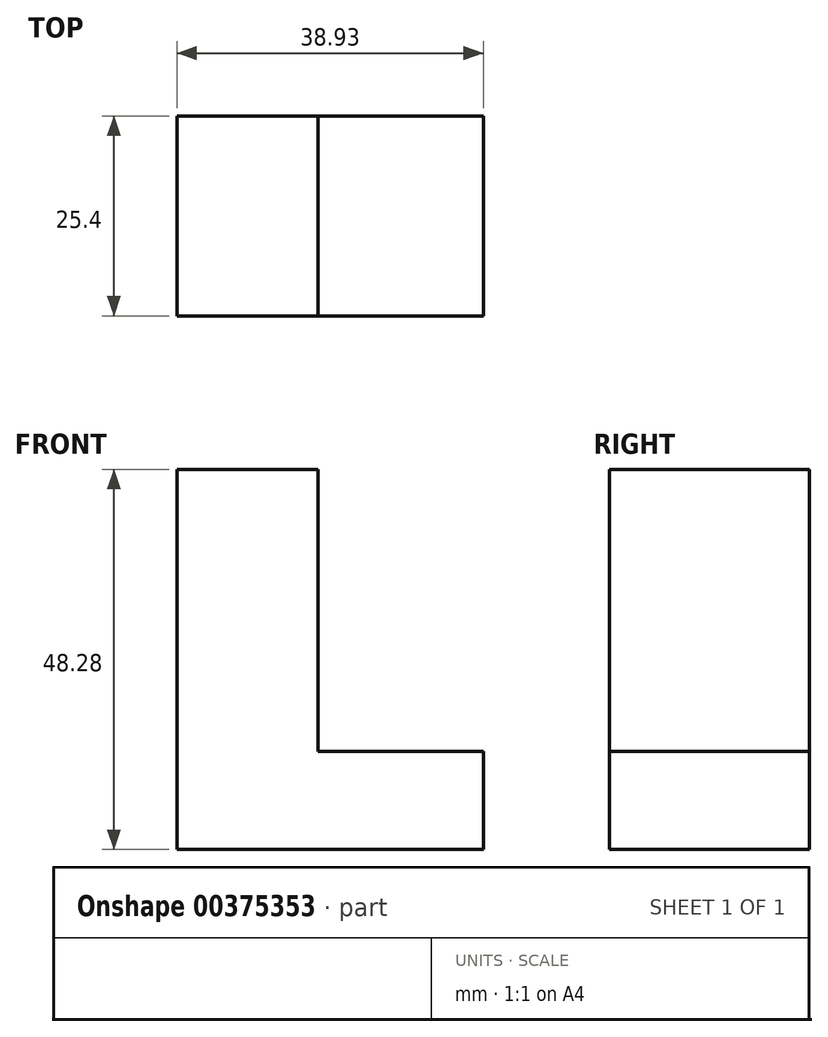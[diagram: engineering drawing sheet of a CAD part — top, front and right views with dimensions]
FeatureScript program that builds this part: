
annotation { "Feature Type Name" : "Feature", "Feature Type Description" : "" }
export const myFeature = defineFeature(function(context is Context, id is Id, definition is map)
    precondition{}
    {
        {
            var Q0;
            Q0=qCreatedBy(makeId("Front.planeOp"),FACE);
            var sketch = newSketch(context, id + "F0", { "sketchPlane" : qUnion([Q0])});
            skLineSegment(sketch, "E0", {"start": v(0, 48.28) * mm, "end": v(0, 0) * mm});
            skLineSegment(sketch, "E1", {"start": v(0, 0) * mm, "end": v(38.93, 0) * mm});
            skLineSegment(sketch, "E2", {"start": v(38.93, 0) * mm, "end": v(38.93, 12.46) * mm});
            skLineSegment(sketch, "E3", {"start": v(38.93, 12.46) * mm, "end": v(17.9, 12.46) * mm});
            skLineSegment(sketch, "E4", {"start": v(0, 48.28) * mm, "end": v(17.9, 48.28) * mm});
            skLineSegment(sketch, "E5", {"start": v(17.9, 48.28) * mm, "end": v(17.9, 12.46) * mm});
            skSolve(sketch);
        }
        {
            var Q0;
            Q0 = qSketchRegion(id + "F0", true);
            extrude(context, id + "F1", {"entities" : qUnion([Q0]), "depth" : 25.4 * mm});
        }
    });
